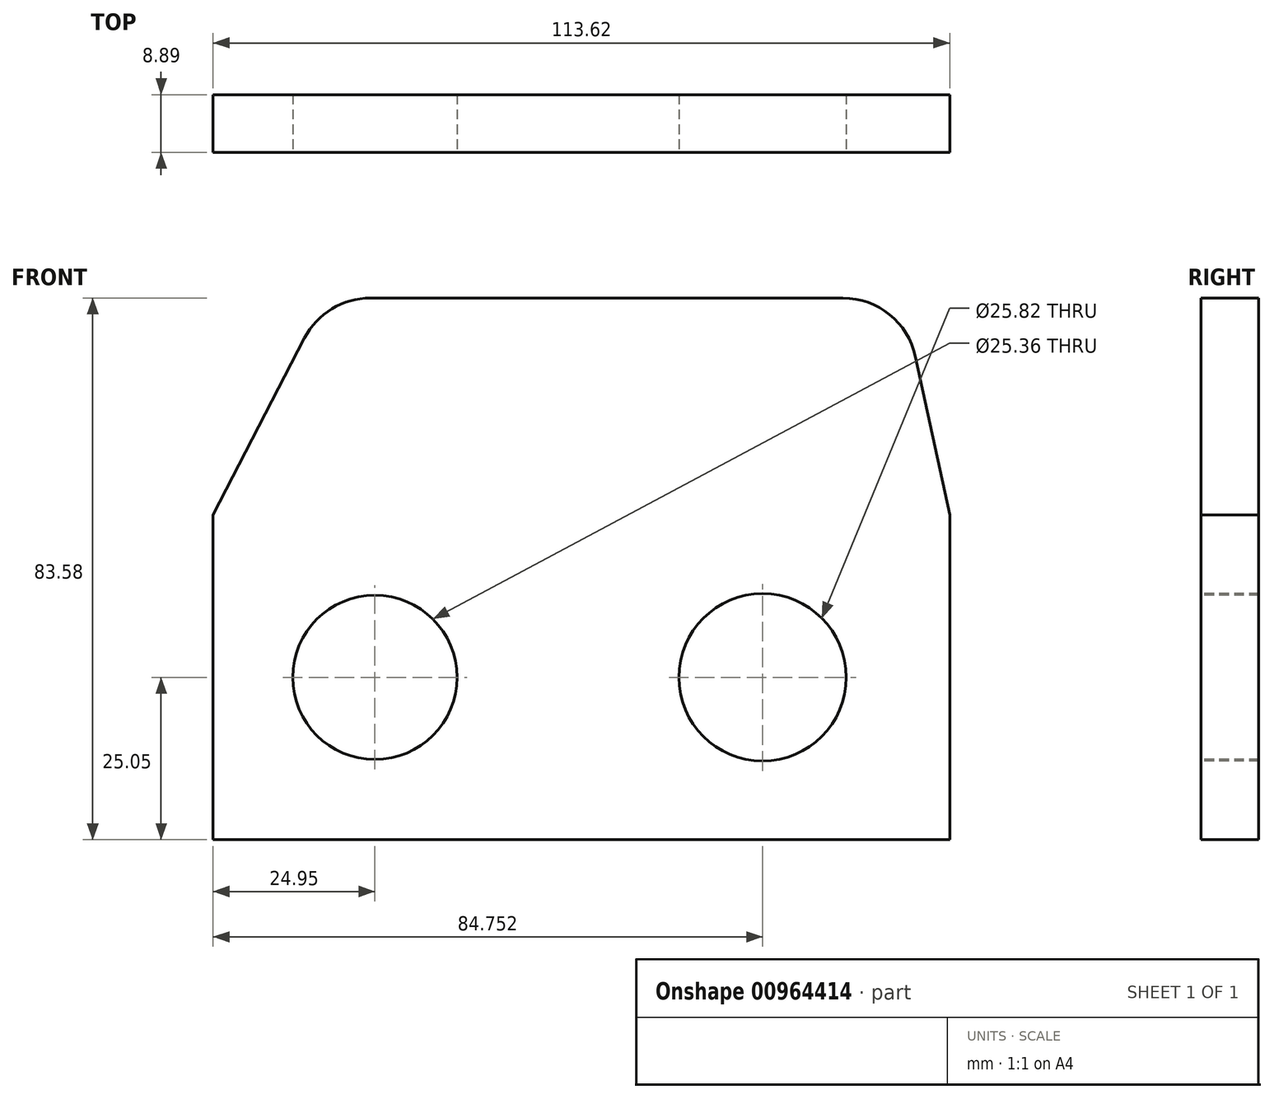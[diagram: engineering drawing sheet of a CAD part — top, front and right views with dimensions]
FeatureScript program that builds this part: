
annotation { "Feature Type Name" : "Feature", "Feature Type Description" : "" }
export const myFeature = defineFeature(function(context is Context, id is Id, definition is map)
    precondition{}
    {
        {
            var Q0;
            Q0=qCreatedBy(makeId("Front.planeOp"),FACE);
            var sketch = newSketch(context, id + "F0", { "sketchPlane" : qUnion([Q0])});
            skLineSegment(sketch, "E0.bottom", {"start": v(-56.81, 25.05) * mm, "end": v(56.81, 25.05) * mm});
            skLineSegment(sketch, "E0.top", {"start": v(-56.81, -25.05) * mm, "end": v(56.81, -25.05) * mm});
            skLineSegment(sketch, "E0.left", {"start": v(-56.81, 25.05) * mm, "end": v(-56.81, -25.05) * mm});
            skLineSegment(sketch, "E0.right", {"start": v(56.81, 25.05) * mm, "end": v(56.81, -25.05) * mm});
            skPoint(sketch, "E0.middle", {"position": v(0, 0) * mm});
            skCircle(sketch, "E1", {"center": v(-31.86, 0) * mm, "radius": 12.68 * mm});
            skCircle(sketch, "E2", {"center": v(27.94, 0) * mm, "radius": 12.91 * mm});
            skLineSegment(sketch, "E3", {"start": v(-56.81, 25.05) * mm, "end": v(-42.7, 52.34) * mm});
            skLineSegment(sketch, "E4", {"start": v(-32.55, 58.53) * mm, "end": v(40.35, 58.53) * mm});
            skLineSegment(sketch, "E5", {"start": v(51.52, 49.51) * mm, "end": v(56.81, 25.05) * mm});
            skPoint(sketch, "E6.visualSharp", {"position": v(-39.51, 58.53) * mm});
            skArc(sketch, "E6.filletArc", {"start": v(-32.55, 58.53) * mm, "mid": v(-38.5, 56.86) * mm, "end": v(-42.7, 52.34) * mm});
            skPoint(sketch, "E7.visualSharp", {"position": v(49.57, 58.53) * mm});
            skArc(sketch, "E7.filletArc", {"start": v(51.52, 49.51) * mm, "mid": v(47.53, 56) * mm, "end": v(40.35, 58.53) * mm});
            skSolve(sketch);
        }
        {
            var Q0;
            Q0 = qSketchRegion(id + "F0", true);
            extrude(context, id + "F1", {"entities" : qUnion([Q0]), "oppositeDirection" : true, "depth" : 8.9 * mm, "offsetDistance" : 25.4 * mm});
        }
    });
